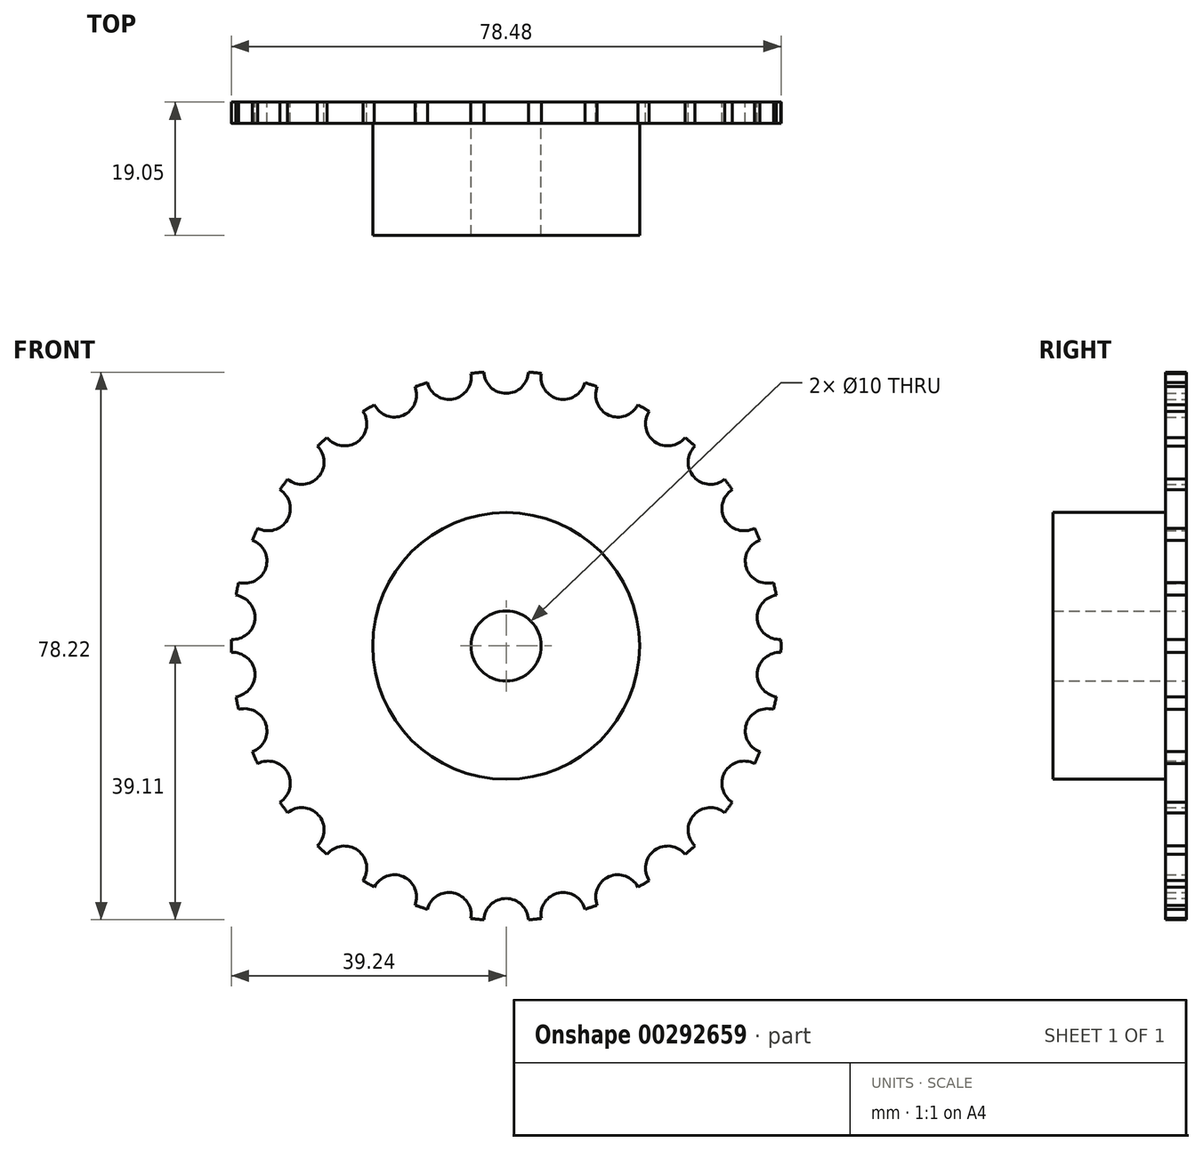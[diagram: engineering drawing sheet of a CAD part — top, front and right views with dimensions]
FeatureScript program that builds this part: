
annotation { "Feature Type Name" : "Feature", "Feature Type Description" : "" }
export const myFeature = defineFeature(function(context is Context, id is Id, definition is map)
    precondition{}
    {
        {
            var Q0;
            Q0=qCreatedBy(makeId("Front.planeOp"),FACE);
            var sketch = newSketch(context, id + "F0", { "sketchPlane" : qUnion([Q0])});
            skCircle(sketch, "E0", {"center": v(0, 0) * mm, "radius": 39.24 * mm});
            skCircle(sketch, "E1", {"center": v(0, 0) * mm, "radius": 19.05 * mm});
            skCircle(sketch, "E2", {"center": v(0, 0) * mm, "radius": 5 * mm});
            skCircle(sketch, "E3", {"center": v(0, 39.24) * mm, "radius": 3.17 * mm});
            skCircle(sketch, "E4.1.0", {"center": v(-8.16, 38.39) * mm, "radius": 3.17 * mm});
            skCircle(sketch, "E4.2.0", {"center": v(-15.96, 35.85) * mm, "radius": 3.17 * mm});
            skCircle(sketch, "E4.3.0", {"center": v(-23.07, 31.75) * mm, "radius": 3.17 * mm});
            skCircle(sketch, "E4.4.0", {"center": v(-29.16, 26.26) * mm, "radius": 3.17 * mm});
            skCircle(sketch, "E4.5.0", {"center": v(-33.99, 19.62) * mm, "radius": 3.17 * mm});
            skCircle(sketch, "E4.6.0", {"center": v(-37.32, 12.13) * mm, "radius": 3.17 * mm});
            skCircle(sketch, "E4.7.0", {"center": v(-39.03, 4.1) * mm, "radius": 3.17 * mm});
            skCircle(sketch, "E4.8.0", {"center": v(-39.03, -4.1) * mm, "radius": 3.17 * mm});
            skCircle(sketch, "E4.9.0", {"center": v(-37.32, -12.13) * mm, "radius": 3.17 * mm});
            skCircle(sketch, "E4.10.0", {"center": v(-33.99, -19.62) * mm, "radius": 3.17 * mm});
            skCircle(sketch, "E4.11.0", {"center": v(-29.16, -26.26) * mm, "radius": 3.17 * mm});
            skCircle(sketch, "E4.12.0", {"center": v(-23.07, -31.75) * mm, "radius": 3.17 * mm});
            skCircle(sketch, "E4.13.0", {"center": v(-15.96, -35.85) * mm, "radius": 3.17 * mm});
            skCircle(sketch, "E4.14.0", {"center": v(-8.16, -38.39) * mm, "radius": 3.17 * mm});
            skCircle(sketch, "E4.15.0", {"center": v(0, -39.24) * mm, "radius": 3.17 * mm});
            skCircle(sketch, "E4.16.0", {"center": v(8.16, -38.39) * mm, "radius": 3.17 * mm});
            skCircle(sketch, "E4.17.0", {"center": v(15.96, -35.85) * mm, "radius": 3.17 * mm});
            skCircle(sketch, "E4.18.0", {"center": v(23.07, -31.75) * mm, "radius": 3.17 * mm});
            skCircle(sketch, "E4.19.0", {"center": v(29.16, -26.26) * mm, "radius": 3.17 * mm});
            skCircle(sketch, "E4.20.0", {"center": v(33.99, -19.62) * mm, "radius": 3.17 * mm});
            skCircle(sketch, "E4.21.0", {"center": v(37.32, -12.13) * mm, "radius": 3.17 * mm});
            skCircle(sketch, "E4.22.0", {"center": v(39.03, -4.1) * mm, "radius": 3.17 * mm});
            skCircle(sketch, "E4.23.0", {"center": v(39.03, 4.1) * mm, "radius": 3.17 * mm});
            skCircle(sketch, "E4.24.0", {"center": v(37.32, 12.13) * mm, "radius": 3.17 * mm});
            skCircle(sketch, "E4.25.0", {"center": v(33.99, 19.62) * mm, "radius": 3.17 * mm});
            skCircle(sketch, "E4.26.0", {"center": v(29.16, 26.26) * mm, "radius": 3.17 * mm});
            skCircle(sketch, "E4.27.0", {"center": v(23.07, 31.75) * mm, "radius": 3.17 * mm});
            skCircle(sketch, "E4.28.0", {"center": v(15.96, 35.85) * mm, "radius": 3.17 * mm});
            skCircle(sketch, "E4.29.0", {"center": v(8.16, 38.39) * mm, "radius": 3.17 * mm});
            skSolve(sketch);
        }
        {
            var Q0;
            Q0=makeQuery(id+"F0.imprint","IMPRINT",FACE,{"disambiguationData":[TD([[makeQuery(id+"F0.imprint","IMPRINT",EDGE,{"derivedFrom":sQuery(id+"F0.wireOp",EDGE,"E1")}),-1.0]])]});
            var Q1;
            Q1=makeQuery(id+"F0.imprint","IMPRINT",FACE,{"disambiguationData":[TD([[makeQuery(id+"F0.imprint","IMPRINT",EDGE,{"derivedFrom":sQuery(id+"F0.wireOp",EDGE,"E1")}),1.0]])]});
            extrude(context, id + "F1", {"entities" : qUnion([Q0, Q1]), "depth" : 3 * mm, "offsetDistance" : 25 * mm});
        }
        {
            var Q0;
            Q0=makeQuery(id+"F0.imprint","IMPRINT",FACE,{"disambiguationData":[TD([[makeQuery(id+"F0.imprint","IMPRINT",EDGE,{"derivedFrom":sQuery(id+"F0.wireOp",EDGE,"E1")}),1.0]])]});
            extrude(context, id + "F2", {"entities" : qUnion([Q0]), "operationType" : NewBodyOperationType.ADD, "depth" : (.75 * 25.4) * mm, "offsetDistance" : 25 * mm});
        }
        {
            var Q0;
            Q0=makeQuery(id+"F1.opExtrude","SWEPT_BODY",BODY,{"disambiguationData":[OSD([sQuery(id+"F0.wireOp",EDGE,"E0"),sQuery(id+"F0.wireOp",EDGE,"E2"),sQuery(id+"F0.wireOp",EDGE,"E3"),sQuery(id+"F0.wireOp",EDGE,"E4.1.0"),sQuery(id+"F0.wireOp",EDGE,"E4.2.0"),sQuery(id+"F0.wireOp",EDGE,"E4.3.0"),sQuery(id+"F0.wireOp",EDGE,"E4.4.0"),sQuery(id+"F0.wireOp",EDGE,"E4.5.0"),sQuery(id+"F0.wireOp",EDGE,"E4.6.0"),sQuery(id+"F0.wireOp",EDGE,"E4.7.0"),sQuery(id+"F0.wireOp",EDGE,"E4.8.0"),sQuery(id+"F0.wireOp",EDGE,"E4.9.0"),sQuery(id+"F0.wireOp",EDGE,"E4.10.0"),sQuery(id+"F0.wireOp",EDGE,"E4.11.0"),sQuery(id+"F0.wireOp",EDGE,"E4.12.0"),sQuery(id+"F0.wireOp",EDGE,"E4.13.0"),sQuery(id+"F0.wireOp",EDGE,"E4.14.0"),sQuery(id+"F0.wireOp",EDGE,"E4.15.0"),sQuery(id+"F0.wireOp",EDGE,"E4.16.0"),sQuery(id+"F0.wireOp",EDGE,"E4.17.0"),sQuery(id+"F0.wireOp",EDGE,"E4.18.0"),sQuery(id+"F0.wireOp",EDGE,"E4.19.0"),sQuery(id+"F0.wireOp",EDGE,"E4.20.0"),sQuery(id+"F0.wireOp",EDGE,"E4.21.0"),sQuery(id+"F0.wireOp",EDGE,"E4.22.0"),sQuery(id+"F0.wireOp",EDGE,"E4.23.0"),sQuery(id+"F0.wireOp",EDGE,"E4.24.0"),sQuery(id+"F0.wireOp",EDGE,"E4.25.0"),sQuery(id+"F0.wireOp",EDGE,"E4.26.0"),sQuery(id+"F0.wireOp",EDGE,"E4.27.0"),sQuery(id+"F0.wireOp",EDGE,"E4.28.0"),sQuery(id+"F0.wireOp",EDGE,"E4.29.0")])]});
            transform(context, id + "F3", {"entities" : qUnion([Q0]), "transformType" : TransformType.TRANSLATION_3D, "dx" : 0 * mm, "dy" : 0 * mm, "dz" : 0 * mm, "makeCopy" : true});
        }
    });
